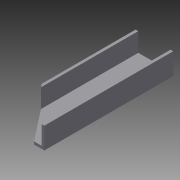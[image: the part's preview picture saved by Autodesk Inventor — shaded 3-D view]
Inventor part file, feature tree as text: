
AUTODESK INVENTOR PART (.ipt)
format: ipt  version: 2015 (Build 190159000, 159)  size: 94,720 bytes
history: native  units: in
note: dims shown in document units (in); Inventor stores cm internally (conversion verified against a paired STEP export)
features: extrude x2, sketch x2, mirror x1
ambient origin geometry x8: Origin, YZ Plane, XZ Plane, XY Plane, X Axis, Y Axis, Z Axis, Center Point
bodies: Solid1 (feature_tree)
feature tree (5):
  extrude  "Extrusion1"  Depth=1.0in
  extrude  "Extrusion4"  Depth=6.0in TaperAngle=0.0deg
  mirror  "Mirror1"
  sketch  "Sketch1"  dims[d0=1.75in d1=1.0in]
  sketch  "Sketch5"  dims[d2=0.125in d3=6.0in d4=0.0in d14=4.375in d15=0.2611in d16=1.0in d17=0.0in]
